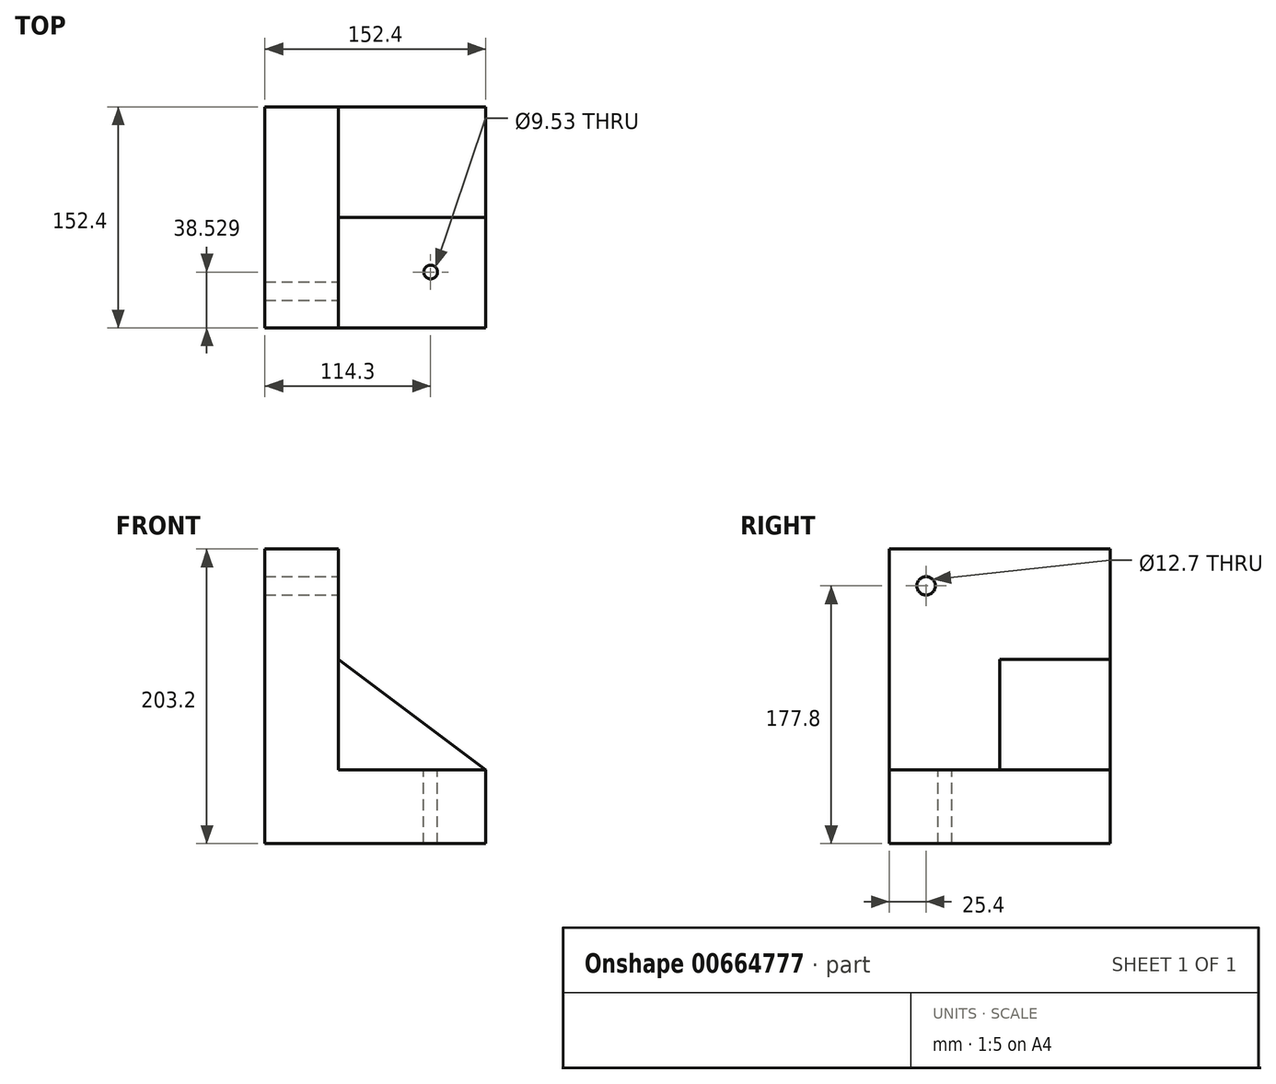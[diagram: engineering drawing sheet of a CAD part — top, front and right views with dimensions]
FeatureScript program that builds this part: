
annotation { "Feature Type Name" : "Feature", "Feature Type Description" : "" }
export const myFeature = defineFeature(function(context is Context, id is Id, definition is map)
    precondition{}
    {
        {
            var Q0;
            Q0=qCreatedBy(makeId("Front.planeOp"),FACE);
            var sketch = newSketch(context, id + "F0", { "sketchPlane" : qUnion([Q0])});
            skLineSegment(sketch, "E0", {"start": v(0, 0) * mm, "end": v(-101.6, 0) * mm});
            skLineSegment(sketch, "E1", {"start": v(-101.6, 0) * mm, "end": v(-101.6, 152.4) * mm});
            skLineSegment(sketch, "E2", {"start": v(-101.6, 152.4) * mm, "end": v(-152.4, 152.4) * mm});
            skLineSegment(sketch, "E3", {"start": v(-152.4, 152.4) * mm, "end": v(-152.4, -50.8) * mm});
            skLineSegment(sketch, "E4", {"start": v(-152.4, -50.8) * mm, "end": v(0, -50.8) * mm});
            skLineSegment(sketch, "E5", {"start": v(0, -50.8) * mm, "end": v(0, 0) * mm});
            skSolve(sketch);
        }
        {
            var Q0;
            Q0 = qSketchRegion(id + "F0", true);
            extrude(context, id + "F1", {"entities" : qUnion([Q0]), "depth" : 152.4 * mm, "offsetDistance" : 25.4 * mm});
        }
        {
            var Q0;
            Q0=makeQuery(id+"F1.opExtrude","SWEPT_FACE",FACE,{"disambiguationData":[OSD([sQuery(id+"F0.wireOp",EDGE,"E0")])]});
            var sketch = newSketch(context, id + "F2", { "sketchPlane" : qUnion([Q0])});
            skLineSegment(sketch, "E6", {"start": v(-101.6, 0) * mm, "end": v(-101.6, -76.2) * mm});
            skLineSegment(sketch, "E7", {"start": v(-101.6, -76.2) * mm, "end": v(0, -76.2) * mm});
            skLineSegment(sketch, "E8", {"start": v(0, -76.2) * mm, "end": v(0, 0) * mm});
            skLineSegment(sketch, "E9", {"start": v(0, 0) * mm, "end": v(-101.6, 0) * mm});
            skSolve(sketch);
        }
        {
            var Q0;
            Q0=makeQuery(id+"F2.imprint","IMPRINT",FACE,{"disambiguationData":[TD([[makeQuery(id+"F2.imprint","IMPRINT",EDGE,{"derivedFrom":sQuery(id+"F2.wireOp",EDGE,"E6")}),-1.0]])]});
            extrude(context, id + "F3", {"entities" : qUnion([Q0]), "operationType" : NewBodyOperationType.ADD, "depth" : 76.2 * mm, "offsetDistance" : 25.4 * mm});
        }
        {
            var Q0;
            Q0=makeQuery(id+"F3.opExtrude","SWEPT_FACE",FACE,{"disambiguationData":[OSD([sQuery(id+"F2.wireOp",EDGE,"E7")])]});
            var sketch = newSketch(context, id + "F4", { "sketchPlane" : qUnion([Q0])});
            skLineSegment(sketch, "E10", {"start": v(-101.6, 76.2) * mm, "end": v(0, 0) * mm});
            skLineSegment(sketch, "E11", {"start": v(0, 0) * mm, "end": v(0, 76.2) * mm});
            skLineSegment(sketch, "E12", {"start": v(0, 76.2) * mm, "end": v(-101.6, 76.2) * mm});
            skSolve(sketch);
        }
        {
            var Q0;
            Q0=makeQuery(id+"F4.imprint","IMPRINT",FACE,{"disambiguationData":[TD([[makeQuery(id+"F4.imprint","IMPRINT",EDGE,{"derivedFrom":sQuery(id+"F4.wireOp",EDGE,"E10")}),1.0]])]});
            extrude(context, id + "F5", {"entities" : qUnion([Q0]), "operationType" : NewBodyOperationType.REMOVE, "oppositeDirection" : true, "depth" : 76.2 * mm, "offsetDistance" : 25.4 * mm});
        }
        {
            var Q0;
            Q0=qCreatedBy(makeId("Top.planeOp"),FACE);
            var sketch = newSketch(context, id + "F6", { "sketchPlane" : qUnion([Q0])});
            skCircle(sketch, "E13", {"center": v(-38.1, -113.87) * mm, "radius": 4.76 * mm});
            skPoint(sketch, "E14.end.orphan", {"position": v(0, -113.87) * mm});
            skPoint(sketch, "E14.start.orphan", {"position": v(0, -151.97) * mm});
            skSolve(sketch);
        }
        {
            var Q0;
            Q0 = qSketchRegion(id + "F6", true);
            extrude(context, id + "F7", {"entities" : qUnion([Q0]), "operationType" : NewBodyOperationType.REMOVE, "oppositeDirection" : true, "depth" : 25.4 * mm, "offsetDistance" : 25.4 * mm});
        }
        {
            var Q0;
            Q0=sQuery(id+"F6.wireOp",VERTEX,"E13.center");
            var Q1;
            Q1=makeQuery(id+"F1.opExtrude","SWEPT_BODY",BODY,{"disambiguationData":[OSD([sQuery(id+"F0.wireOp",EDGE,"E0"),sQuery(id+"F0.wireOp",EDGE,"E1"),sQuery(id+"F0.wireOp",EDGE,"E2"),sQuery(id+"F0.wireOp",EDGE,"E3"),sQuery(id+"F0.wireOp",EDGE,"E4"),sQuery(id+"F0.wireOp",EDGE,"E5")])]});
            hole(context, id + "F8", {"style" : HoleStyle.SIMPLE, "endStyle" : HoleEndStyle.THROUGH, "holeDiameter" : 9.52 * mm, "majorDiameter" : 6.35 * mm, "isTappedThrough" : true, "tappedDepth" : 12.7 * mm, "tapClearance" : 3, "locations" : qUnion([Q0]), "scope" : qUnion([Q1])});
        }
        {
            var Q0;
            Q0=makeQuery(id+"F1.opExtrude","SWEPT_FACE",FACE,{"disambiguationData":[OSD([sQuery(id+"F0.wireOp",EDGE,"E1")])]});
            var sketch = newSketch(context, id + "F9", { "sketchPlane" : qUnion([Q0])});
            skPoint(sketch, "E15", {"position": v(-127, 127) * mm});
            skPoint(sketch, "E16", {"position": v(-204.58, 235.08) * mm});
            skCircle(sketch, "E17", {"center": v(-127, 127) * mm, "radius": 9.53 * mm});
            skSolve(sketch);
        }
        {
            var Q0;
            Q0=sQuery(id+"F9.wireOp",VERTEX,"E15");
            var Q1;
            Q1=makeQuery(id+"F1.opExtrude","SWEPT_BODY",BODY,{"disambiguationData":[OSD([sQuery(id+"F0.wireOp",EDGE,"E0"),sQuery(id+"F0.wireOp",EDGE,"E1"),sQuery(id+"F0.wireOp",EDGE,"E2"),sQuery(id+"F0.wireOp",EDGE,"E3"),sQuery(id+"F0.wireOp",EDGE,"E4"),sQuery(id+"F0.wireOp",EDGE,"E5")])]});
            hole(context, id + "F10", {"style" : HoleStyle.SIMPLE, "endStyle" : HoleEndStyle.THROUGH, "holeDiameter" : 12.7 * mm, "majorDiameter" : 6.35 * mm, "isTappedThrough" : true, "tappedDepth" : 12.7 * mm, "tapClearance" : 3, "locations" : qUnion([Q0]), "scope" : qUnion([Q1])});
        }
    });
